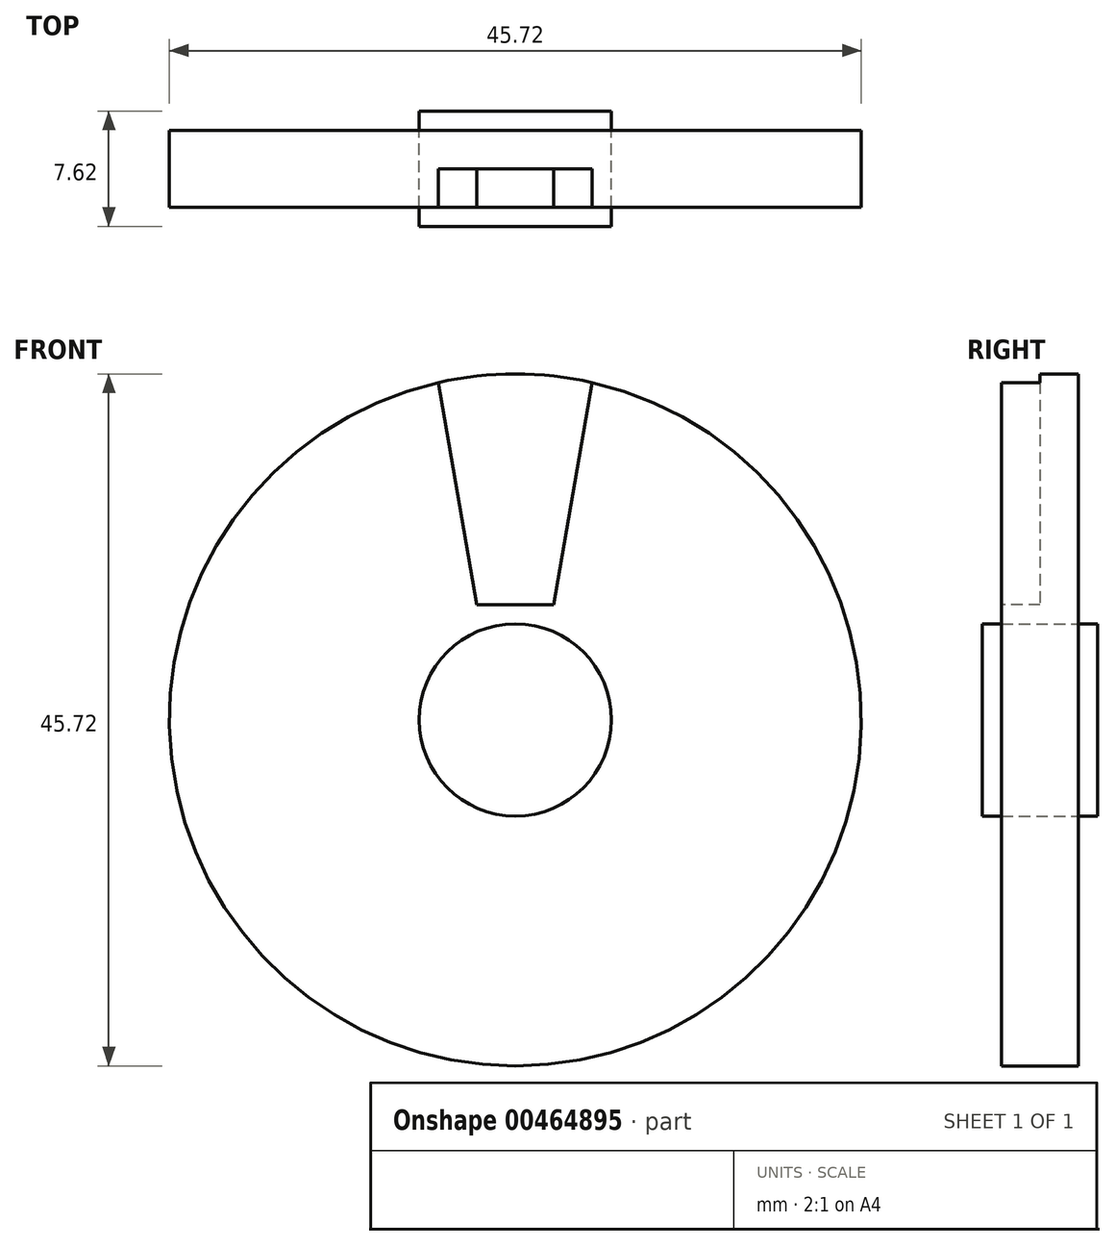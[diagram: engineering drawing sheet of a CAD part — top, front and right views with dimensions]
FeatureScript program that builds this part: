
annotation { "Feature Type Name" : "Feature", "Feature Type Description" : "" }
export const myFeature = defineFeature(function(context is Context, id is Id, definition is map)
    precondition{}
    {
        {
            var Q0;
            Q0=qCreatedBy(makeId("Front.planeOp"),FACE);
            var sketch = newSketch(context, id + "F0", { "sketchPlane" : qUnion([Q0])});
            skCircle(sketch, "E0", {"center": v(0, 0) * mm, "radius": 6.35 * mm});
            skSolve(sketch);
        }
        {
            var Q0;
            Q0=qCreatedBy(makeId("Front.planeOp"),FACE);
            var sketch = newSketch(context, id + "F1", { "sketchPlane" : qUnion([Q0])});
            skCircle(sketch, "E1", {"center": v(0, 0) * mm, "radius": 22.86 * mm});
            skSolve(sketch);
        }
        {
            var Q0;
            Q0 = qSketchRegion(id + "F0", true);
            extrude(context, id + "F2", {"entities" : qUnion([Q0]), "endBound" : BoundingType.SYMMETRIC, "depth" : 7.62 * mm});
        }
        {
            var Q0;
            Q0=makeQuery(id+"F1.imprint","IMPRINT",FACE,{"disambiguationData":[TD([[makeQuery(id+"F1.imprint","IMPRINT",EDGE,{"derivedFrom":sQuery(id+"F1.wireOp",EDGE,"E1")}),1.0]])]});
            extrude(context, id + "F3", {"entities" : qUnion([Q0]), "endBound" : BoundingType.SYMMETRIC, "depth" : 5.08 * mm});
        }
        {
            var Q0;
            Q0=makeQuery(id+"F3.opExtrude","CAP_FACE",FACE,{"disambiguationData":[OSD([sQuery(id+"F1.wireOp",EDGE,"E1")])],"isStart":false});
            var sketch = newSketch(context, id + "F4", { "sketchPlane" : qUnion([Q0])});
            skLineSegment(sketch, "E2", {"start": v(-2.54, 7.62) * mm, "end": v(2.54, 7.62) * mm});
            skLineSegment(sketch, "E3", {"start": v(-5.08, 22.29) * mm, "end": v(-2.54, 7.62) * mm});
            skLineSegment(sketch, "E4", {"start": v(5.08, 22.29) * mm, "end": v(2.54, 7.62) * mm});
            skSolve(sketch);
        }
        {
            var Q0;
            Q0=makeQuery(id+"F4.imprint","IMPRINT",FACE,{"disambiguationData":[TD([[makeQuery(id+"F4.imprint","IMPRINT",EDGE,{"derivedFrom":sQuery(id+"F4.wireOp",EDGE,"E2")}),1.0]])]});
            extrude(context, id + "F5", {"entities" : qUnion([Q0]), "operationType" : NewBodyOperationType.REMOVE, "oppositeDirection" : true, "depth" : 2.54 * mm});
        }
    });
